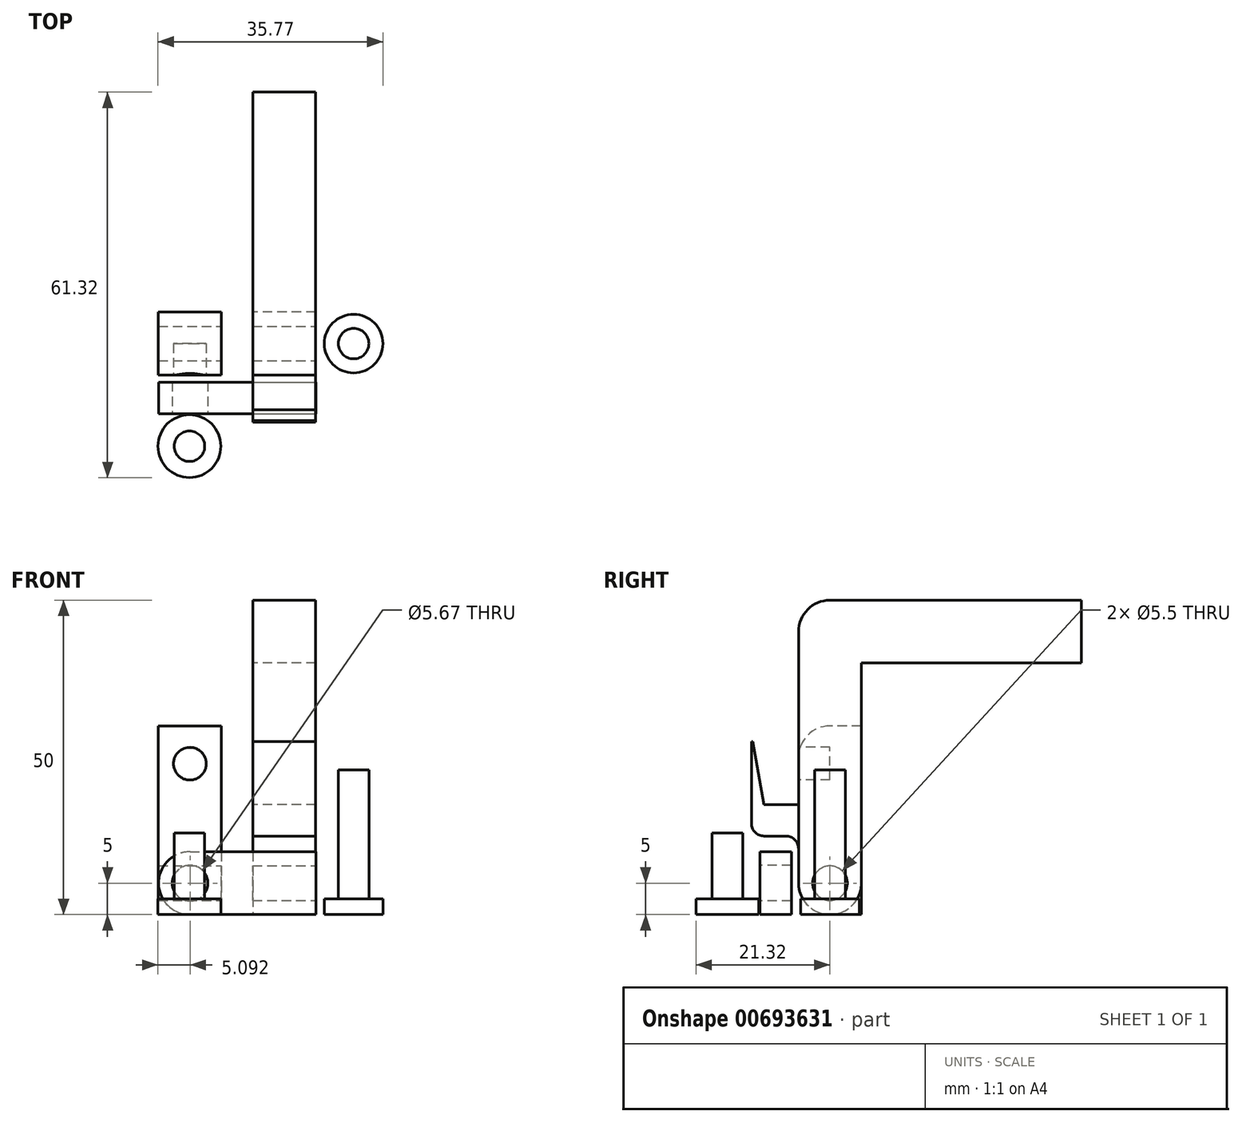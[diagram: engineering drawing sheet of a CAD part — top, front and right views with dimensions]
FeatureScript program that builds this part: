
annotation { "Feature Type Name" : "Feature", "Feature Type Description" : "" }
export const myFeature = defineFeature(function(context is Context, id is Id, definition is map)
    precondition{}
    {
        {
            var Q0;
            Q0=qCreatedBy(makeId("Top.planeOp"),FACE);
            var sketch = newSketch(context, id + "F0", { "sketchPlane" : qUnion([Q0])});
            skLineSegment(sketch, "E0.bottom", {"start": v(5, 5) * mm, "end": v(-5, 5) * mm});
            skLineSegment(sketch, "E0.top", {"start": v(5, -5) * mm, "end": v(-5, -5) * mm});
            skLineSegment(sketch, "E0.left", {"start": v(5, 5) * mm, "end": v(5, -5) * mm});
            skLineSegment(sketch, "E0.right", {"start": v(-5, 5) * mm, "end": v(-5, -5) * mm});
            skPoint(sketch, "E0.middle", {"position": v(0, 0) * mm});
            skSolve(sketch);
        }
        {
            var Q0;
            Q0=makeQuery(id+"F0.imprint","IMPRINT",FACE,{"disambiguationData":[TD([[makeQuery(id+"F0.imprint","IMPRINT",EDGE,{"derivedFrom":sQuery(id+"F0.wireOp",EDGE,"E0.bottom")}),1.0]])]});
            extrude(context, id + "F1", {"entities" : qUnion([Q0]), "depth" : 50 * mm, "offsetDistance" : 25 * mm});
        }
        {
            var Q0;
            Q0=makeQuery(id+"F1.opExtrude","SWEPT_FACE",FACE,{"disambiguationData":[OSD([sQuery(id+"F0.wireOp",EDGE,"E0.bottom")])]});
            var sketch = newSketch(context, id + "F2", { "sketchPlane" : qUnion([Q0])});
            skLineSegment(sketch, "E1.bottom", {"start": v(-5, 50) * mm, "end": v(5, 50) * mm});
            skLineSegment(sketch, "E1.top", {"start": v(-5, 40) * mm, "end": v(5, 40) * mm});
            skLineSegment(sketch, "E1.left", {"start": v(-5, 50) * mm, "end": v(-5, 40) * mm});
            skLineSegment(sketch, "E1.right", {"start": v(5, 50) * mm, "end": v(5, 40) * mm});
            skSolve(sketch);
        }
        {
            var Q0;
            Q0=makeQuery(id+"F2.imprint","IMPRINT",FACE,{"disambiguationData":[TD([[makeQuery(id+"F2.imprint","IMPRINT",EDGE,{"derivedFrom":sQuery(id+"F2.wireOp",EDGE,"E1.bottom")}),-1.0]])]});
            extrude(context, id + "F3", {"entities" : qUnion([Q0]), "operationType" : NewBodyOperationType.ADD, "depth" : 35 * mm, "offsetDistance" : 25 * mm});
        }
        {
            var Q0;
            Q0=makeQuery(id+"F1.opExtrude","CAP_EDGE",EDGE,{"disambiguationData":[OSD([sQuery(id+"F0.wireOp",EDGE,"E0.top")])],"isStart":false});
            var Q1;
            Q1=makeQuery(id+"F3.opExtrude","CAP_EDGE",EDGE,{"disambiguationData":[OSD([sQuery(id+"F2.wireOp",EDGE,"E1.top")])],"isStart":true});
            fillet(context, id + "F4", {"entities" : qUnion([Q0, Q1]), "radius" : 5 * mm, "tangentPropagation" : true, "allowEdgeOverflow" : false});
        }
        {
            var Q0;
            Q0=makeQuery(id+"F1.opExtrude","SWEPT_FACE",FACE,{"disambiguationData":[OSD([sQuery(id+"F0.wireOp",EDGE,"E0.top")])]});
            var sketch = newSketch(context, id + "F5", { "sketchPlane" : qUnion([Q0])});
            skLineSegment(sketch, "E2.bottom", {"start": v(5, 17.5) * mm, "end": v(-5, 17.5) * mm});
            skLineSegment(sketch, "E2.top", {"start": v(5, 12.5) * mm, "end": v(-5, 12.5) * mm});
            skLineSegment(sketch, "E2.left", {"start": v(5, 17.5) * mm, "end": v(5, 12.5) * mm});
            skLineSegment(sketch, "E2.right", {"start": v(-5, 17.5) * mm, "end": v(-5, 12.5) * mm});
            skPoint(sketch, "E2.middle", {"position": v(0, 15) * mm});
            skPoint(sketch, "E2.middle.positionSnap0", {"position": v(-5, 22.5) * mm});
            skPoint(sketch, "E2.middle.positionSnap1", {"position": v(0, 45) * mm});
            skPoint(sketch, "E2.centerSnap0", {"position": v(-5, 22.5) * mm});
            skPoint(sketch, "E2.centerSnap1", {"position": v(0, 45) * mm});
            skSolve(sketch);
        }
        {
            var Q0;
            Q0=makeQuery(id+"F5.imprint","IMPRINT",FACE,{"disambiguationData":[TD([[makeQuery(id+"F5.imprint","IMPRINT",EDGE,{"derivedFrom":sQuery(id+"F5.wireOp",EDGE,"E2.bottom")}),1.0]])]});
            extrude(context, id + "F6", {"entities" : qUnion([Q0]), "operationType" : NewBodyOperationType.ADD, "depth" : 7.5 * mm, "offsetDistance" : 25 * mm});
        }
        {
            var Q0;
            Q0=makeQuery(id+"F6.opExtrude","SWEPT_FACE",FACE,{"disambiguationData":[OSD([sQuery(id+"F5.wireOp",EDGE,"E2.bottom")])]});
            var sketch = newSketch(context, id + "F7", { "sketchPlane" : qUnion([Q0])});
            skLineSegment(sketch, "E3.bottom", {"start": v(-5, -12.5) * mm, "end": v(5, -12.5) * mm});
            skLineSegment(sketch, "E3.top", {"start": v(-5, -10.5) * mm, "end": v(5, -10.5) * mm});
            skLineSegment(sketch, "E3.left", {"start": v(-5, -12.5) * mm, "end": v(-5, -10.5) * mm});
            skLineSegment(sketch, "E3.right", {"start": v(5, -12.5) * mm, "end": v(5, -10.5) * mm});
            skSolve(sketch);
        }
        {
            var Q0;
            Q0=makeQuery(id+"F7.imprint","IMPRINT",FACE,{"disambiguationData":[TD([[makeQuery(id+"F7.imprint","IMPRINT",EDGE,{"derivedFrom":sQuery(id+"F7.wireOp",EDGE,"E3.bottom")}),-1.0]])]});
            extrude(context, id + "F8", {"entities" : qUnion([Q0]), "operationType" : NewBodyOperationType.ADD, "depth" : 10 * mm, "offsetDistance" : 25 * mm});
        }
        {
            var Q0;
            Q0=makeQuery(id+"F8.opExtrude","CAP_EDGE",EDGE,{"disambiguationData":[OSD([sQuery(id+"F7.wireOp",EDGE,"E3.top")])],"isStart":false});
            chamfer(context, id + "F9", {"entities" : qUnion([Q0]), "chamferType" : ChamferType.OFFSET_ANGLE, "width" : 10 * mm, "oppositeDirection" : false, "angle" : 10 * degree, "tangentPropagation" : true});
        }
        {
            var Q0;
            Q0=makeQuery(id+"F6.opExtrude","CAP_EDGE",EDGE,{"disambiguationData":[OSD([sQuery(id+"F5.wireOp",EDGE,"E2.top")])],"isStart":true});
            var Q1;
            Q1=makeQuery(id+"F6.opExtrude","CAP_EDGE",EDGE,{"disambiguationData":[OSD([sQuery(id+"F5.wireOp",EDGE,"E2.top")])],"isStart":false});
            fillet(context, id + "F10", {"entities" : qUnion([Q0, Q1]), "radius" : 2 * mm, "tangentPropagation" : true, "allowEdgeOverflow" : false});
        }
        {
            var Q0;
            Q0=qCreatedBy(makeId("Top.planeOp"),FACE);
            var sketch = newSketch(context, id + "F11", { "sketchPlane" : qUnion([Q0])});
            skLineSegment(sketch, "E4.bottom", {"start": v(-10, 5) * mm, "end": v(-20, 5) * mm});
            skLineSegment(sketch, "E4.top", {"start": v(-10, -5) * mm, "end": v(-20, -5) * mm});
            skLineSegment(sketch, "E4.left", {"start": v(-10, 5) * mm, "end": v(-10, -5) * mm});
            skLineSegment(sketch, "E4.right", {"start": v(-20, 5) * mm, "end": v(-20, -5) * mm});
            skPoint(sketch, "E4.middle", {"position": v(-15, 0) * mm});
            skSolve(sketch);
        }
        {
            var Q0;
            Q0=makeQuery(id+"F11.imprint","IMPRINT",FACE,{"disambiguationData":[TD([[makeQuery(id+"F11.imprint","IMPRINT",EDGE,{"derivedFrom":sQuery(id+"F11.wireOp",EDGE,"E4.bottom")}),1.0]])]});
            extrude(context, id + "F12", {"entities" : qUnion([Q0]), "depth" : 30 * mm, "offsetDistance" : 25 * mm});
        }
        {
            var Q0;
            Q0=makeQuery(id+"F12.opExtrude","SWEPT_FACE",FACE,{"disambiguationData":[OSD([sQuery(id+"F11.wireOp",EDGE,"E4.left")])]});
            var sketch = newSketch(context, id + "F13", { "sketchPlane" : qUnion([Q0])});
            skCircle(sketch, "E5", {"center": v(0, 5) * mm, "radius": 2.6 * mm});
            skSolve(sketch);
        }
        {
            var Q0;
            Q0=makeQuery(id+"F8.boolean.opBoolean","MERGE",FACE,{"derivedFrom":[makeQuery(id+"F6.boolean.opBoolean","MERGE",FACE,{"derivedFrom":[makeQuery(id+"F3.boolean.opBoolean","MERGE",FACE,{"derivedFrom":[makeQuery(id+"F1.opExtrude","SWEPT_FACE",FACE,{"disambiguationData":[OSD([sQuery(id+"F0.wireOp",EDGE,"E0.left")])]}),makeQuery(id+"F3.opExtrude","SWEPT_FACE",FACE,{"disambiguationData":[OSD([sQuery(id+"F2.wireOp",EDGE,"E1.left")])]})]}),makeQuery(id+"F6.opExtrude","SWEPT_FACE",FACE,{"disambiguationData":[OSD([sQuery(id+"F5.wireOp",EDGE,"E2.left")])]})]}),makeQuery(id+"F8.opExtrude","SWEPT_FACE",FACE,{"disambiguationData":[OSD([sQuery(id+"F7.wireOp",EDGE,"E3.right")])]})]});
            var sketch = newSketch(context, id + "F14", { "sketchPlane" : qUnion([Q0])});
            skCircle(sketch, "E6", {"center": v(0, 5) * mm, "radius": 2.75 * mm});
            skSolve(sketch);
        }
        {
            var Q0;
            Q0=makeQuery(id+"F14.imprint","IMPRINT",FACE,{"disambiguationData":[TD([[makeQuery(id+"F14.imprint","IMPRINT",EDGE,{"derivedFrom":sQuery(id+"F14.wireOp",EDGE,"E6")}),1.0]])]});
            extrude(context, id + "F15", {"entities" : qUnion([Q0]), "operationType" : NewBodyOperationType.REMOVE, "oppositeDirection" : true, "depth" : 25 * mm, "offsetDistance" : 25 * mm});
        }
        {
            var Q0;
            Q0=makeQuery(id+"F13.imprint","IMPRINT",FACE,{"disambiguationData":[TD([[makeQuery(id+"F13.imprint","IMPRINT",EDGE,{"derivedFrom":sQuery(id+"F13.wireOp",EDGE,"E5")}),1.0]])]});
            extrude(context, id + "F16", {"entities" : qUnion([Q0]), "operationType" : NewBodyOperationType.REMOVE, "oppositeDirection" : true, "depth" : 10 * mm, "offsetDistance" : 25 * mm});
        }
        {
            var Q0;
            Q0=makeQuery(id+"F12.opExtrude","SWEPT_FACE",FACE,{"disambiguationData":[OSD([sQuery(id+"F11.wireOp",EDGE,"E4.top")])]});
            var sketch = newSketch(context, id + "F17", { "sketchPlane" : qUnion([Q0])});
            skCircle(sketch, "E7", {"center": v(-15, 24) * mm, "radius": 2.6 * mm});
            skPoint(sketch, "E7.centerSnap0", {"position": v(-15, 30) * mm});
            skSolve(sketch);
        }
        {
            var Q0;
            Q0=makeQuery(id+"F17.imprint","IMPRINT",FACE,{"disambiguationData":[TD([[makeQuery(id+"F17.imprint","IMPRINT",EDGE,{"derivedFrom":sQuery(id+"F17.wireOp",EDGE,"E7")}),1.0]])]});
            extrude(context, id + "F18", {"entities" : qUnion([Q0]), "operationType" : NewBodyOperationType.REMOVE, "oppositeDirection" : true, "depth" : 5 * mm, "offsetDistance" : 25 * mm});
        }
        {
            var Q0;
            Q0=qCreatedBy(makeId("Top.planeOp"),FACE);
            var sketch = newSketch(context, id + "F19", { "sketchPlane" : qUnion([Q0])});
            skLineSegment(sketch, "E8.bottom", {"start": v(-19.98, -6.14) * mm, "end": v(5.02, -6.14) * mm});
            skLineSegment(sketch, "E8.top", {"start": v(-19.98, -11.14) * mm, "end": v(5.02, -11.14) * mm});
            skLineSegment(sketch, "E8.left", {"start": v(-19.98, -6.14) * mm, "end": v(-19.98, -11.14) * mm});
            skLineSegment(sketch, "E8.right", {"start": v(5.02, -6.14) * mm, "end": v(5.02, -11.14) * mm});
            skSolve(sketch);
        }
        {
            var Q0;
            Q0=makeQuery(id+"F19.imprint","IMPRINT",FACE,{"disambiguationData":[TD([[makeQuery(id+"F19.imprint","IMPRINT",EDGE,{"derivedFrom":sQuery(id+"F19.wireOp",EDGE,"E8.bottom")}),-1.0]])]});
            extrude(context, id + "F20", {"entities" : qUnion([Q0]), "depth" : 10 * mm, "offsetDistance" : 25 * mm});
        }
        {
            var Q0;
            Q0=makeQuery(id+"F20.opExtrude","SWEPT_FACE",FACE,{"disambiguationData":[OSD([sQuery(id+"F19.wireOp",EDGE,"E8.top")])]});
            var sketch = newSketch(context, id + "F21", { "sketchPlane" : qUnion([Q0])});
            skCircle(sketch, "E9", {"center": v(-14.98, 5) * mm, "radius": 2.83 * mm});
            skPoint(sketch, "E9.centerSnap0", {"position": v(-19.98, 5) * mm});
            skSolve(sketch);
        }
        {
            var Q0;
            Q0=makeQuery(id+"F21.imprint","IMPRINT",FACE,{"disambiguationData":[TD([[makeQuery(id+"F21.imprint","IMPRINT",EDGE,{"derivedFrom":sQuery(id+"F21.wireOp",EDGE,"E9")}),1.0]])]});
            extrude(context, id + "F22", {"entities" : qUnion([Q0]), "operationType" : NewBodyOperationType.REMOVE, "oppositeDirection" : true, "depth" : 5 * mm, "offsetDistance" : 25 * mm});
        }
        {
            var Q0;
            Q0=qCreatedBy(makeId("Top.planeOp"),FACE);
            var sketch = newSketch(context, id + "F23", { "sketchPlane" : qUnion([Q0])});
            skCircle(sketch, "E10", {"center": v(11.04, 0) * mm, "radius": 2.43 * mm});
            skSolve(sketch);
        }
        {
            var Q0;
            Q0=makeQuery(id+"F23.imprint","IMPRINT",FACE,{"disambiguationData":[TD([[makeQuery(id+"F23.imprint","IMPRINT",EDGE,{"derivedFrom":sQuery(id+"F23.wireOp",EDGE,"E10")}),1.0]])]});
            extrude(context, id + "F24", {"entities" : qUnion([Q0]), "depth" : (10 + 5 + 5 + 3) * mm, "offsetDistance" : 25 * mm});
        }
        {
            var Q0;
            Q0=makeQuery(id+"F24.opExtrude","CAP_FACE",FACE,{"disambiguationData":[OSD([sQuery(id+"F23.wireOp",EDGE,"E10")])],"isStart":true});
            var sketch = newSketch(context, id + "F25", { "sketchPlane" : qUnion([Q0])});
            skCircle(sketch, "E11", {"center": v(11.04, 0) * mm, "radius": 4.66 * mm});
            skSolve(sketch);
        }
        {
            var Q0;
            Q0=makeQuery(id+"F25.imprint","IMPRINT",FACE,{"disambiguationData":[TD([[makeQuery(id+"F25.imprint","IMPRINT",EDGE,{"derivedFrom":sQuery(id+"F25.wireOp",EDGE,"E11")}),1.0]])]});
            extrude(context, id + "F26", {"entities" : qUnion([Q0]), "operationType" : NewBodyOperationType.ADD, "oppositeDirection" : true, "depth" : 2.5 * mm, "offsetDistance" : 25 * mm});
        }
        {
            var Q0;
            Q0=qCreatedBy(makeId("Top.planeOp"),FACE);
            var sketch = newSketch(context, id + "F27", { "sketchPlane" : qUnion([Q0])});
            skCircle(sketch, "E12", {"center": v(-15.07, -16.32) * mm, "radius": 2.43 * mm});
            skSolve(sketch);
        }
        {
            var Q0;
            Q0=makeQuery(id+"F27.imprint","IMPRINT",FACE,{"disambiguationData":[TD([[makeQuery(id+"F27.imprint","IMPRINT",EDGE,{"derivedFrom":sQuery(id+"F27.wireOp",EDGE,"E12")}),1.0]])]});
            extrude(context, id + "F28", {"entities" : qUnion([Q0]), "depth" : (5 + 5 + 3) * mm, "offsetDistance" : 25 * mm});
        }
        {
            var Q0;
            Q0=makeQuery(id+"F28.opExtrude","CAP_FACE",FACE,{"disambiguationData":[OSD([sQuery(id+"F27.wireOp",EDGE,"E12")])],"isStart":true});
            var sketch = newSketch(context, id + "F29", { "sketchPlane" : qUnion([Q0])});
            skCircle(sketch, "E13", {"center": v(-15.07, 16.32) * mm, "radius": 5 * mm});
            skSolve(sketch);
        }
        {
            var Q0;
            Q0 = qSketchRegion(id + "F29", true);
            extrude(context, id + "F30", {"entities" : qUnion([Q0]), "operationType" : NewBodyOperationType.ADD, "oppositeDirection" : true, "depth" : 2.5 * mm, "offsetDistance" : 25 * mm});
        }
        {
            var Q0;
            Q0=makeQuery(id+"F1.opExtrude","CAP_EDGE",EDGE,{"disambiguationData":[OSD([sQuery(id+"F0.wireOp",EDGE,"E0.bottom")])],"isStart":true});
            var Q1;
            Q1=makeQuery(id+"F1.opExtrude","CAP_EDGE",EDGE,{"disambiguationData":[OSD([sQuery(id+"F0.wireOp",EDGE,"E0.top")])],"isStart":true});
            fillet(context, id + "F31", {"entities" : qUnion([Q0, Q1]), "radius" : 5 * mm, "tangentPropagation" : true, "allowEdgeOverflow" : false});
        }
        {
            var Q0;
            Q0=makeQuery(id+"F20.opExtrude","CAP_EDGE",EDGE,{"disambiguationData":[OSD([sQuery(id+"F19.wireOp",EDGE,"E8.left")])],"isStart":false});
            var Q1;
            Q1=makeQuery(id+"F20.opExtrude","CAP_EDGE",EDGE,{"disambiguationData":[OSD([sQuery(id+"F19.wireOp",EDGE,"E8.left")])],"isStart":true});
            fillet(context, id + "F32", {"entities" : qUnion([Q0, Q1]), "radius" : 5 * mm, "tangentPropagation" : true, "allowEdgeOverflow" : false});
        }
        {
            var Q0;
            Q0=makeQuery(id+"F12.opExtrude","CAP_EDGE",EDGE,{"disambiguationData":[OSD([sQuery(id+"F11.wireOp",EDGE,"E4.top")])],"isStart":true});
            var Q1;
            Q1=makeQuery(id+"F12.opExtrude","CAP_EDGE",EDGE,{"disambiguationData":[OSD([sQuery(id+"F11.wireOp",EDGE,"E4.top")])],"isStart":false});
            fillet(context, id + "F33", {"entities" : qUnion([Q0, Q1]), "radius" : 5 * mm, "tangentPropagation" : true, "allowEdgeOverflow" : false});
        }
    });
